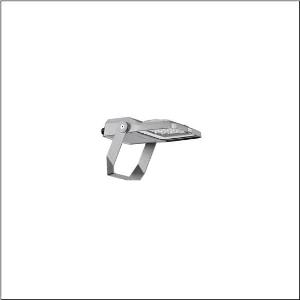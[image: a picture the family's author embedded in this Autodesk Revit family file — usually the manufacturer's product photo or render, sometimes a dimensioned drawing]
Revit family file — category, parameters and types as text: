
# Revit family: floodlight_fl_21_iq_micro___rs12_5xa7762a1b1a_c11c
name_source: partatom
category: Lighting Fixtures
units: mm (PartAtom-declared; Revit-internal decimal feet)

## family parameters
Cut with Voids When Loaded = No
Host = Face
Light Source = No
Part Type = Normal
Room Calculation Point = No
Round Connector Dimension = Use Diameter
Shared = No

## types (1)
- --- (1 x LED, 2560 lm, 23.1 W, 2200K)
    Apparent Load = 23 VA
    CIE Flux Codes = 79 92 99 100 100
    Color Rendering = 70
    Color Temperature = 2200K
    Default Elevation = 1800 mm
    Description = Floodlight FL 21 iQ micro, floodlight, primary light control with lens, of PMMA, primary optical cover: protective disc, of toughened safety glass, transparent, light distribution: RS12, light emission: direct distribution, installation type: surface-mounted, LED, High Power LED, rated luminous flux: 2.560lm, luminous efficacy: 111lm/W, light colour: 722, colour temperature: 2200K, control: Auto-Match, Temp-Guard, Night-Set, Smart-Wire, Desk-Remote (wireless, voltage-free reading and setting of iQ features in the workshop via application-optimized NFC function/RFID function), optimised constant luminous flux control (CLO 2.0), Street-Remote, with terminal, 6-pole, mains connection: 220..240V, AC, 50/60Hz, start of lifetime: 23W, end of service life: 24W, reduction: 11W, luminaire housing, of diecast aluminium, powder-coated, Siteco® metallic grey (DB 702S), corrosivity category C5 mid according to DIN EN ISO 12944, sealing non-destructively replaceable, mounting bracket, of steel, galvanised, powder-coated, Siteco® metallic grey (DB 702S), protection rating (complete): IP66, insulation class (complete): insulation class II (safety insulation), certification: CE, ENEC, VDE, protection symbol: D, impact resistance: IK07, permissible operating ambient temperature: -40..+40°C, permissible operating ambient temperature for outdoor applications: -40..+50°C, standard: DIN EN 12944, LABS conformity tested according to VDMA 24364:2018-05, packaging unit: 1 piece

Light Distribution: RS12
    Height = 65 mm
    Lamp = 1 x LED
    Lamp Light Flux = 2560 lm
    Lamp Power = 23.1 W
    Lamp count = 1
    Length = 312 mm
    Luminous efficacy = 111 lm/W
    Manufacturer = Siteco
    ModVariant = No
    Model = 5XA7762A1B1A
    Number of Poles = 1
    OnlyDefault = Yes
    Power Factor = 1
    Product Name = Floodlight FL 21 iQ micro | RS12
    Product group = floodlight | pylon annexe
    ProductGroupID = 6200
    Protection Class = Protection class II
    Protection Degree = IP 66
    RLX_Detail_Level = 1
    RLX_Emergency_Light_Flux = 0 lm
    RLX_Emergency_Type = 0
    RLX_Emergency_Type_DB = No
    RlxData = <blob elided: 75141 chars, md5=f0c0d542>
    Socket = socket
    Standby Power = 0 W
    System Light Flux = 2560 lm
    System Power = 23 W
    Type Comments = factory setting: luminous flux: 100 % | dim-lin: 254 | 455 mA
    Type Image = l_1006880.jpg
    URL = http://relux.com
    VarID = @adj_133305
    Voltage = 0 V
    Weight = 0.00 kg
    Width = 230 mm

## geometry (parser evidence)
native form markers: Blend x4, Sweep x12
no freeform markers — native parametric forms only
